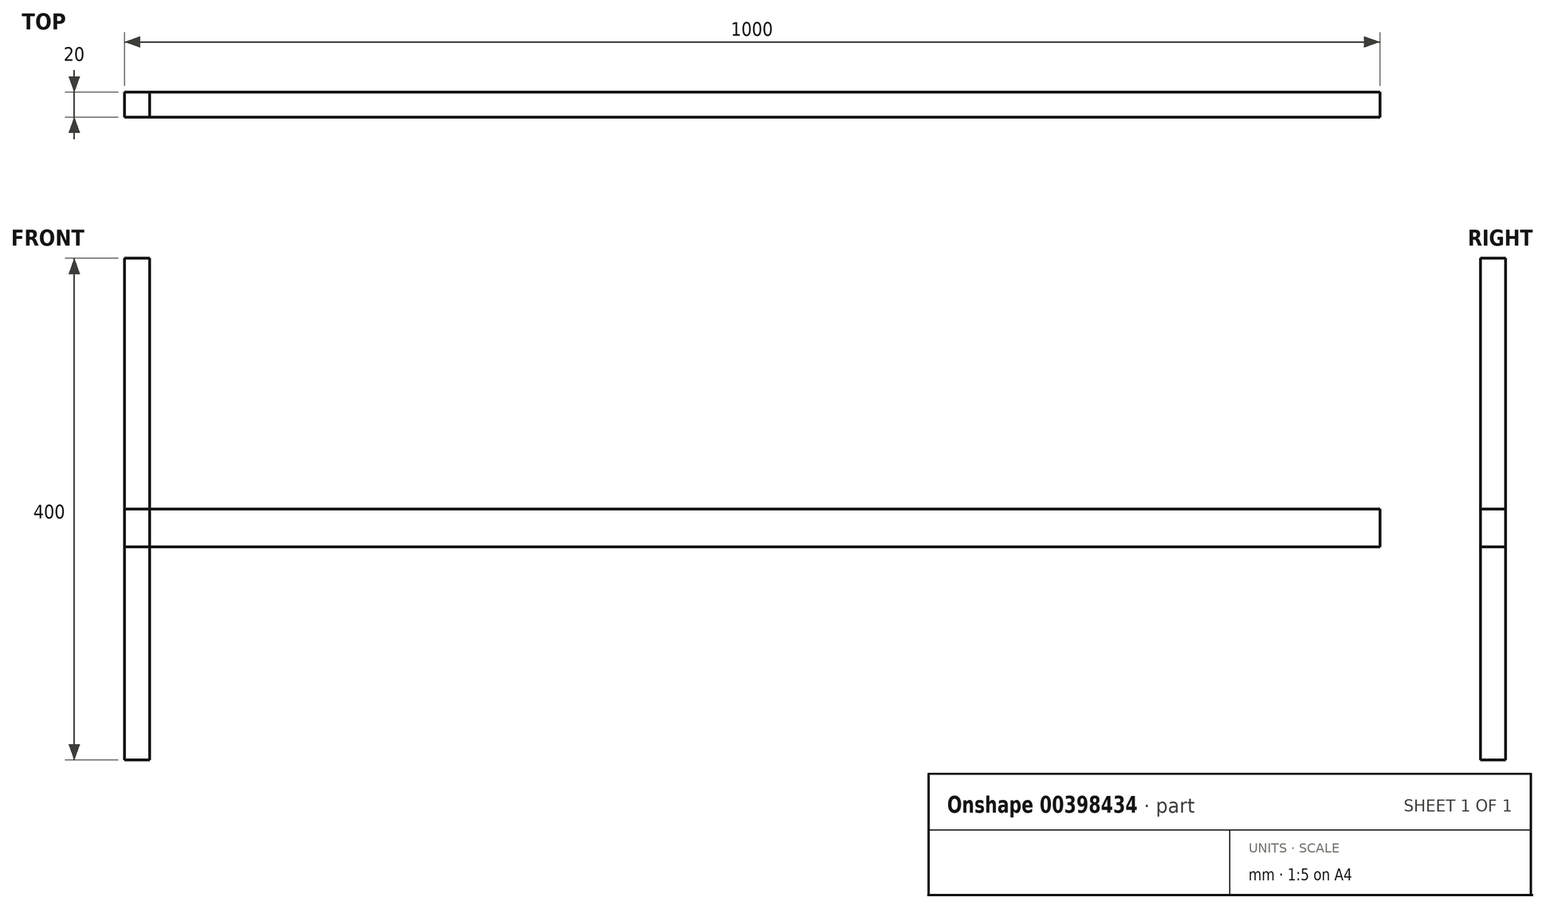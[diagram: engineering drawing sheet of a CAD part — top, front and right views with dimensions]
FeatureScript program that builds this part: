
annotation { "Feature Type Name" : "Feature", "Feature Type Description" : "" }
export const myFeature = defineFeature(function(context is Context, id is Id, definition is map)
    precondition{}
    {
        {
            var Q0;
            Q0=qCreatedBy(makeId("Front.planeOp"),FACE);
            var sketch = newSketch(context, id + "F0", { "sketchPlane" : qUnion([Q0])});
            skLineSegment(sketch, "E0.bottom", {"start": v(-500, 400) * mm, "end": v(0, 400) * mm});
            skLineSegment(sketch, "E0.top", {"start": v(-500, 370) * mm, "end": v(0, 370) * mm});
            skLineSegment(sketch, "E0.left", {"start": v(-500, 400) * mm, "end": v(-500, 370) * mm});
            skLineSegment(sketch, "E1.top", {"start": v(-500, 0) * mm, "end": v(-480, 0) * mm});
            skLineSegment(sketch, "E2.bottom", {"start": v(-500, 200) * mm, "end": v(0, 200) * mm});
            skLineSegment(sketch, "E2.top", {"start": v(-500, 170) * mm, "end": v(0, 170) * mm});
            skLineSegment(sketch, "E2.left", {"start": v(-500, 200) * mm, "end": v(-500, 170) * mm});
            skLineSegment(sketch, "E3", {"start": v(-500, 370) * mm, "end": v(-500, 200) * mm});
            skLineSegment(sketch, "E4", {"start": v(-500, 170) * mm, "end": v(-500, 0) * mm});
            skLineSegment(sketch, "E5", {"start": v(-480, 0) * mm, "end": v(-480, 170) * mm});
            skLineSegment(sketch, "E6", {"start": v(-480, 170) * mm, "end": v(-480, 200) * mm});
            skLineSegment(sketch, "E7", {"start": v(-480, 200) * mm, "end": v(-480, 370) * mm});
            skLineSegment(sketch, "E8", {"start": v(-480, 355) * mm, "end": v(-480, 415) * mm});
            skLineSegment(sketch, "E9", {"start": v(-500, 385) * mm, "end": v(-480, 385) * mm, "construction": true});
            skPoint(sketch, "E10", {"position": v(-490, 385) * mm});
            skLineSegment(sketch, "E11", {"start": v(-500, 185) * mm, "end": v(-480, 185) * mm, "construction": true});
            skPoint(sketch, "E12", {"position": v(-490, 185) * mm});
            skLineSegment(sketch, "E13", {"start": v(-192.5, 311.33) * mm, "end": v(-192.5, 258.67) * mm});
            skLineSegment(sketch, "E14", {"start": v(-192.5, 258.67) * mm, "end": v(-480, 200) * mm});
            skPoint(sketch, "E15", {"position": v(-192.5, 285) * mm});
            skLineSegment(sketch, "E16", {"start": v(0, 400) * mm, "end": v(0, 170) * mm, "construction": true});
            skPoint(sketch, "E17", {"position": v(0, 285) * mm});
            skLineSegment(sketch, "E18", {"start": v(-490, 385) * mm, "end": v(0, 285) * mm, "construction": true});
            skLineSegment(sketch, "E19", {"start": v(-490, 185) * mm, "end": v(0, 285) * mm, "construction": true});
            skLineSegment(sketch, "E20", {"start": v(-192.5, 311.33) * mm, "end": v(-480, 370) * mm});
            skLineSegment(sketch, "E21.MirrorCS", {"start": v(500, 400) * mm, "end": v(0, 400) * mm});
            skLineSegment(sketch, "E22.MirrorCS", {"start": v(500, 370) * mm, "end": v(0, 370) * mm});
            skLineSegment(sketch, "E23.MirrorCS", {"start": v(500, 200) * mm, "end": v(0, 200) * mm});
            skLineSegment(sketch, "E24.MirrorCS", {"start": v(500, 170) * mm, "end": v(0, 170) * mm});
            skLineSegment(sketch, "E25.MirrorCS", {"start": v(500, 400) * mm, "end": v(500, 370) * mm});
            skLineSegment(sketch, "E26.MirrorCS", {"start": v(480, 355) * mm, "end": v(480, 415) * mm});
            skLineSegment(sketch, "E27.MirrorCS", {"start": v(480, 200) * mm, "end": v(480, 370) * mm});
            skLineSegment(sketch, "E28.MirrorCS", {"start": v(500, 370) * mm, "end": v(500, 200) * mm});
            skLineSegment(sketch, "E29.MirrorCS", {"start": v(480, 170) * mm, "end": v(480, 200) * mm});
            skLineSegment(sketch, "E30.MirrorCS", {"start": v(500, 200) * mm, "end": v(500, 170) * mm});
            skLineSegment(sketch, "E31.MirrorCS", {"start": v(480, 0) * mm, "end": v(480, 170) * mm});
            skLineSegment(sketch, "E32.MirrorCS", {"start": v(500, 170) * mm, "end": v(500, 0) * mm});
            skLineSegment(sketch, "E33.MirrorCS", {"start": v(500, 0) * mm, "end": v(480, 0) * mm});
            skPoint(sketch, "E34.MirrorP", {"position": v(490, 185) * mm});
            skPoint(sketch, "E35.MirrorP", {"position": v(490, 385) * mm});
            skLineSegment(sketch, "E36.MirrorCS", {"start": v(192.5, 311.33) * mm, "end": v(480, 370) * mm});
            skLineSegment(sketch, "E37.MirrorCS", {"start": v(192.5, 258.67) * mm, "end": v(480, 200) * mm});
            skLineSegment(sketch, "E38.MirrorCS", {"start": v(192.5, 311.33) * mm, "end": v(192.5, 258.67) * mm});
            skSolve(sketch);
        }
        {
            var Q0;
            {var subQ0=sQuery(id+"F0.wireOp",EDGE,"E0.left");Q0=makeQuery(id+"F0.imprint","IMPRINT",FACE,{"disambiguationData":[TD([[makeQuery(id+"F0.imprint","IMPRINT",EDGE,{"derivedFrom":subQ0}),1.0]])]});}
            var Q1;
            {var subQ0=sQuery(id+"F0.wireOp",EDGE,"E3");Q1=makeQuery(id+"F0.imprint","IMPRINT",FACE,{"disambiguationData":[TD([[makeQuery(id+"F0.imprint","IMPRINT",EDGE,{"derivedFrom":subQ0}),1.0]])]});}
            var Q2;
            Q2=makeQuery(id+"F0.imprint","IMPRINT",FACE,{"disambiguationData":[TD([[makeQuery(id+"F0.imprint","IMPRINT",EDGE,{"derivedFrom":sQuery(id+"F0.wireOp",EDGE,"E1.top")}),1.0]])]});
            var Q3;
            {var subQ0=sQuery(id+"F0.wireOp",EDGE,"E2.left");Q3=makeQuery(id+"F0.imprint","IMPRINT",FACE,{"disambiguationData":[TD([[makeQuery(id+"F0.imprint","IMPRINT",EDGE,{"derivedFrom":subQ0}),1.0]])]});}
            extrude(context, id + "F1", {"entities" : qUnion([Q0, Q1, Q2, Q3]), "oppositeDirection" : true, "depth" : 20 * mm});
        }
        {
            var Q0;
            {var subQ4=sQuery(id+"F0.wireOp",EDGE,"E6");Q0=makeQuery(id+"F0.imprint","IMPRINT",FACE,{"disambiguationData":[TD([[makeQuery(id+"F0.imprint","IMPRINT",EDGE,{"derivedFrom":subQ4}),-1.0]])]});}
            var Q1;
            {var subQ0=sQuery(id+"F0.wireOp",EDGE,"E2.left");Q1=makeQuery(id+"F0.imprint","IMPRINT",FACE,{"disambiguationData":[TD([[makeQuery(id+"F0.imprint","IMPRINT",EDGE,{"derivedFrom":subQ0}),1.0]])]});}
            var Q2;
            {var subQ0=sQuery(id+"F0.wireOp",EDGE,"3711527e-29d4-454f-b52b-14dabd29da080.MirrorCS");Q2=makeQuery(id+"F0.imprint","IMPRINT",FACE,{"disambiguationData":[TD([[makeQuery(id+"F0.imprint","IMPRINT",EDGE,{"derivedFrom":subQ0}),-1.0]])]});}
            var Q3;
            {var subQ2=sQuery(id+"F0.wireOp",EDGE,"E29.MirrorCS");Q3=makeQuery(id+"F0.imprint","IMPRINT",FACE,{"disambiguationData":[TD([[makeQuery(id+"F0.imprint","IMPRINT",EDGE,{"derivedFrom":subQ2}),-1.0]])]});}
            extrude(context, id + "F2", {"entities" : qUnion([Q0, Q1, Q2, Q3]), "oppositeDirection" : true, "depth" : 20 * mm});
        }
    });
